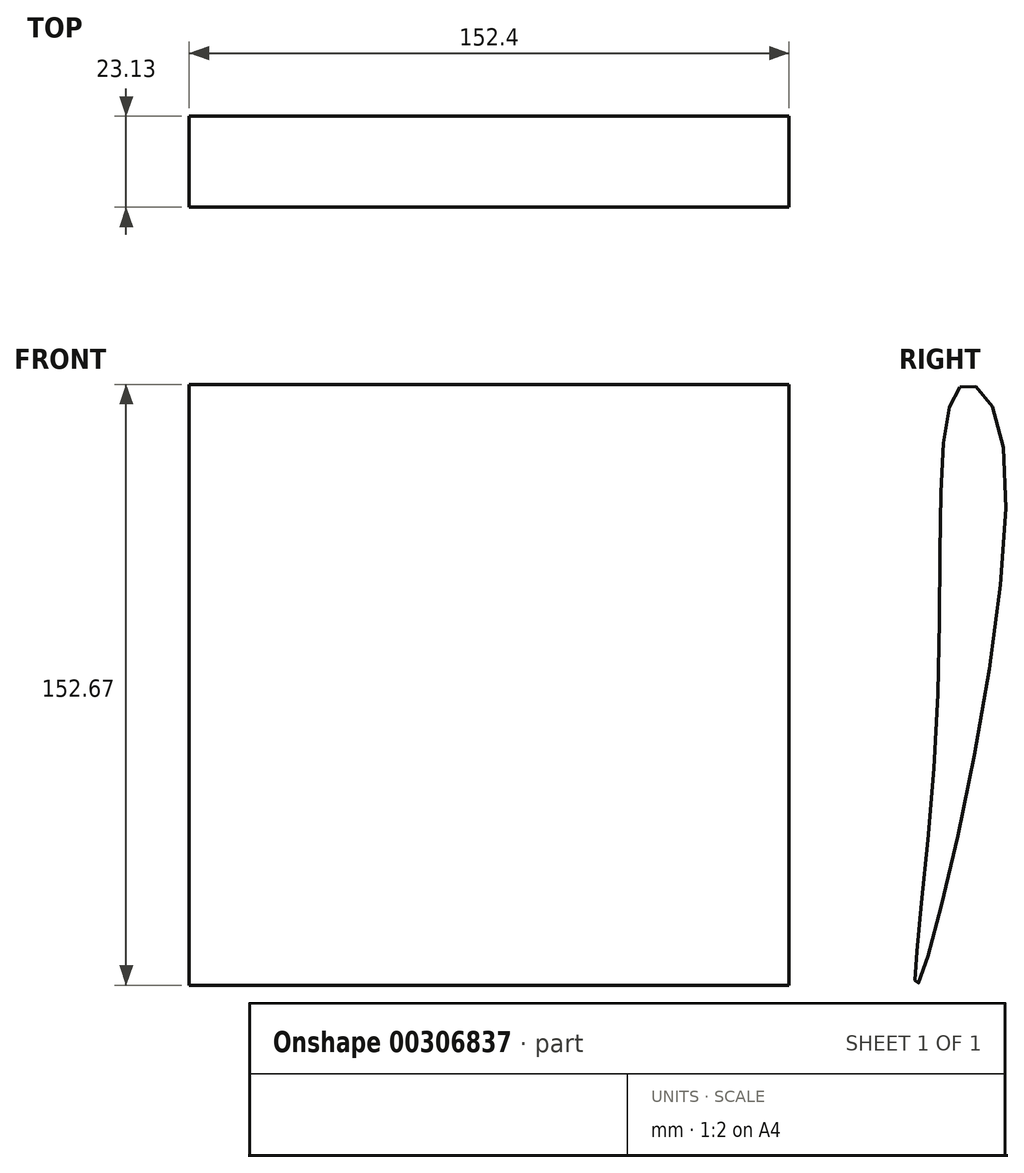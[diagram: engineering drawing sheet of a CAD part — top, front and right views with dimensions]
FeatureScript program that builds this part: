
annotation { "Feature Type Name" : "Feature", "Feature Type Description" : "" }
export const myFeature = defineFeature(function(context is Context, id is Id, definition is map)
    precondition{}
    {
        {
            var Q0;
            Q0=qCreatedBy(makeId("Right.planeOp"),FACE);
            var sketch = newSketch(context, id + "F0", { "sketchPlane" : qUnion([Q0])});
            skFitSpline(sketch, "E0", {"points": [v(8.56, 74.97) * mm, v(19.4, 61.14) * mm, v(-2.03, -76.46) * mm, v(2.7, -8.93) * mm, v(8.56, 74.97) * mm]});
            skSolve(sketch);
        }
        {
            var Q0;
            Q0=makeQuery(id+"F0.imprint","IMPRINT",FACE,{"disambiguationData":[TD([[makeQuery(id+"F0.imprint","IMPRINT",EDGE,{"derivedFrom":sQuery(id+"F0.wireOp",EDGE,"E0")}),-1.0]])]});
            extrude(context, id + "F1", {"entities" : qUnion([Q0]), "depth" : 76.2 * mm, "hasSecondDirection" : true, "secondDirectionOppositeDirection" : true, "secondDirectionDepth" : 76.2 * mm});
        }
    });
